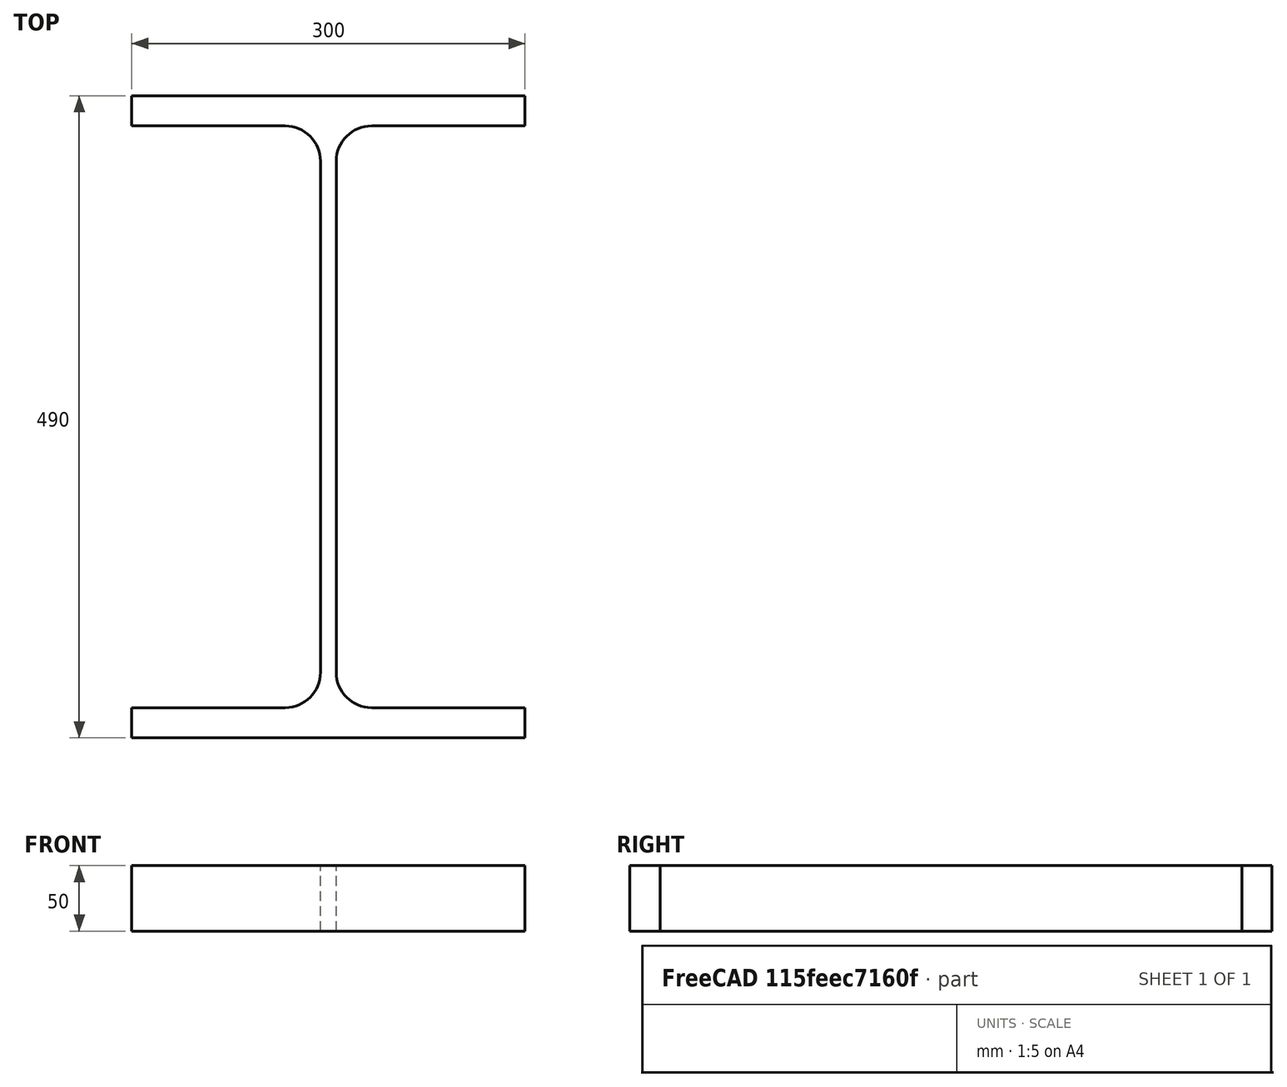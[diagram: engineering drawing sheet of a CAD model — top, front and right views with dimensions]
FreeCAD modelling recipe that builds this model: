
FCSTD DOCUMENT  (FreeCAD 0.15R4671 (Git))
Label: HE-A-Profile 500 DIN1025-3 S235JR
License: All rights reserved
LicenseURL: http://en.wikipedia.org/wiki/All_rights_reserved
objects: Sketcher::SketchObject×1, Part::Extrusion×1
note: 2 computed .brp shape members not serialized (recipe doc carries the construction recipe); baked Part::Feature solids carry a one-line shape summary decoded from their .brp

FEATURE [Sketcher::SketchObject] Sketch
  sketch-geometry (16):
    g0: LineSegment StartX=6 StartY=-195 StartZ=0 EndX=6 EndY=195 EndZ=0
    g1: LineSegment StartX=33 StartY=222 StartZ=0 EndX=150 EndY=222 EndZ=0
    g2: LineSegment StartX=150 StartY=222 StartZ=0 EndX=150 EndY=245 EndZ=0
    g3: LineSegment StartX=150 StartY=245 StartZ=0 EndX=-150 EndY=245 EndZ=0
    g4: LineSegment StartX=-150 StartY=245 StartZ=0 EndX=-150 EndY=222 EndZ=0
    g5: LineSegment StartX=-150 StartY=222 StartZ=0 EndX=-33 EndY=222 EndZ=0
    g6: LineSegment StartX=-6 StartY=195 StartZ=0 EndX=-6 EndY=-195 EndZ=0
    g7: LineSegment StartX=-33 StartY=-222 StartZ=0 EndX=-150 EndY=-222 EndZ=0
    g8: LineSegment StartX=-150 StartY=-222 StartZ=0 EndX=-150 EndY=-245 EndZ=0
    g9: LineSegment StartX=-150 StartY=-245 StartZ=0 EndX=150 EndY=-245 EndZ=0
    g10: LineSegment StartX=150 StartY=-245 StartZ=0 EndX=150 EndY=-222 EndZ=0
    g11: LineSegment StartX=150 StartY=-222 StartZ=0 EndX=33 EndY=-222 EndZ=0
    g12: ArcOfCircle CenterX=33 CenterY=195 CenterZ=0 NormalX=0 NormalY=0 NormalZ=1 Radius=27 StartAngle=1.5708 EndAngle=3.14159
    g13: ArcOfCircle CenterX=33 CenterY=-195 CenterZ=0 NormalX=0 NormalY=0 NormalZ=1 Radius=27 StartAngle=3.14159 EndAngle=4.71239
    g14: ArcOfCircle CenterX=-33 CenterY=195 CenterZ=0 NormalX=0 NormalY=0 NormalZ=1 Radius=27 StartAngle=0 EndAngle=1.5708
    g15: ArcOfCircle CenterX=-33 CenterY=-195 CenterZ=0 NormalX=0 NormalY=0 NormalZ=1 Radius=27 StartAngle=4.71239 EndAngle=6.28319
  constraints (42):
    c: Vertical(g0)
    c: Coincident(g2,g1)
    c: Vertical(g2)
    c: Coincident(g3,g2)
    c: Coincident(g4,g3)
    c: Vertical(g4)
    c: Coincident(g5,g4)
    c: Horizontal(g5)
    c: Vertical(g6)
    c: Horizontal(g7)
    c: Coincident(g8,g7)
    c: Vertical(g8)
    c: Coincident(g9,g8)
    c: Horizontal(g9)
    c: Coincident(g10,g9)
    c: Vertical(g10)
    c: Coincident(g11,g10)
    c: Horizontal(g11)
    c: Tangent(g1,g12) = 1.5708
    c: Tangent(g0,g12) = 1.5708
    c: Tangent(g0,g13) = 1.5708
    c: Tangent(g11,g13) = 1.5708
    c: Tangent(g5,g14) = 1.5708
    c: Tangent(g6,g14) = 1.5708
    c: Tangent(g6,g15) = 1.5708
    c: Tangent(g7,g15) = 1.5708
    c: Equal(g3,g9)
    c: Equal(g2,g4)
    c: Equal(g4,g8)
    c: Equal(g8,g10)
    c: Equal(g12,g14)
    c: Equal(g14,g15)
    c: Equal(g15,g13)
    c: Symmetric(g2,g3,g-2)
    c: Symmetric(g9,g8,g-2)
    c: Symmetric(g0,g6,g-2)
    c: Symmetric(g2,g9,g-1)
    c: DistanceY(g2,g9) = -490
    c: DistanceX(g3) = -300
    c: DistanceX(g0,g6) = -12
    c: DistanceY(g2) = 23
    c: Radius(g12) = 27
FEATURE [Part::Extrusion] Extrude  label="HE-A-Profile 500 DIN1025-3 S235JR"
  Base = -> Sketch
  Dir = (0,0,50)
  Solid = true
